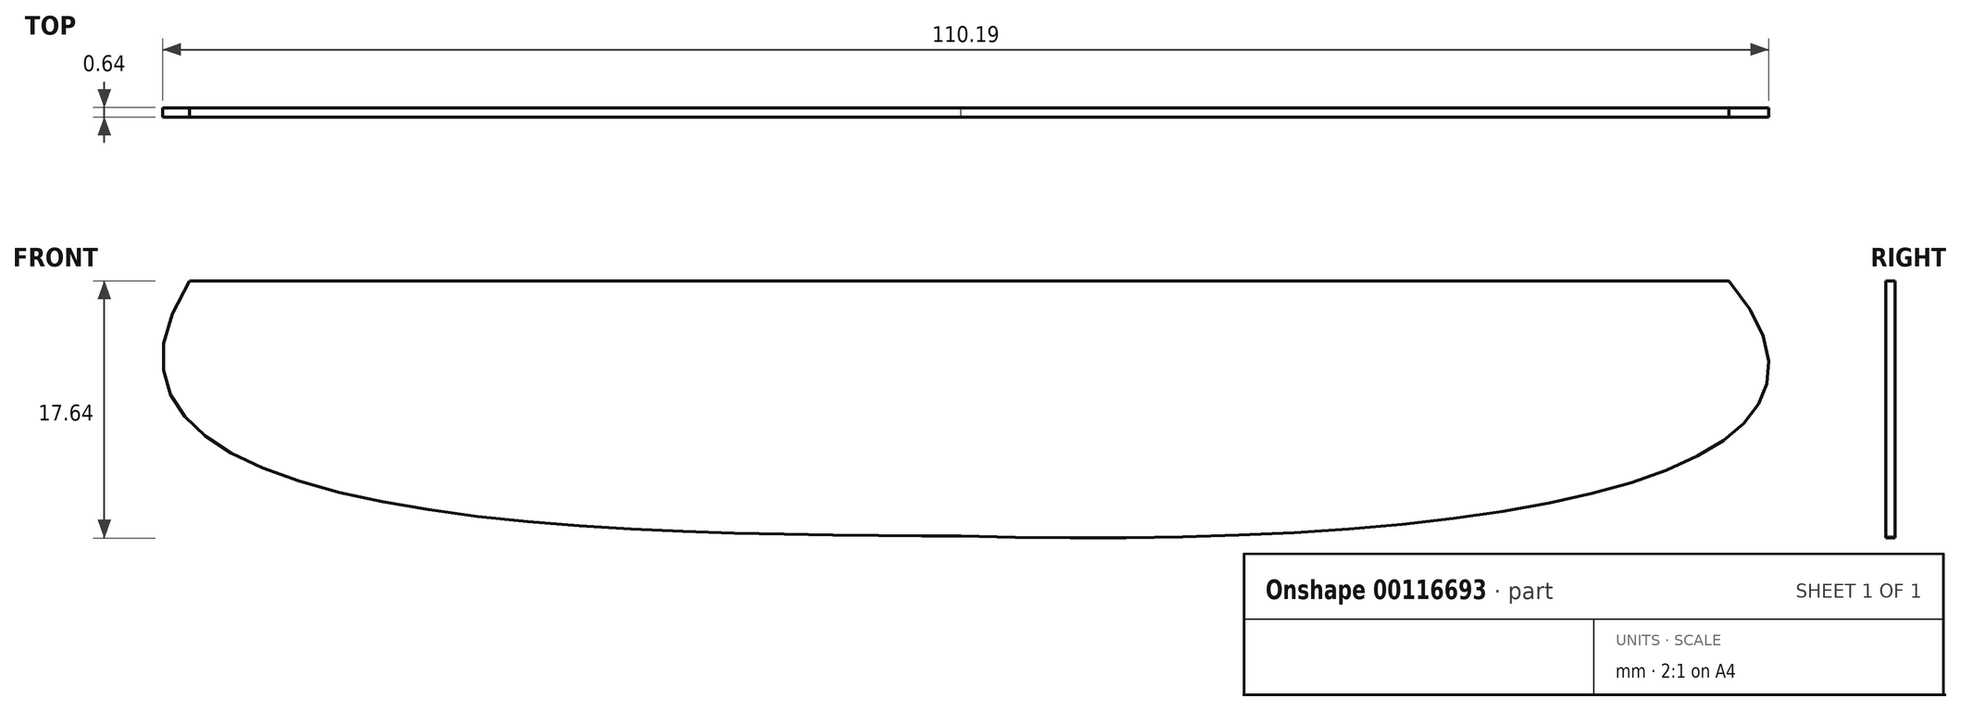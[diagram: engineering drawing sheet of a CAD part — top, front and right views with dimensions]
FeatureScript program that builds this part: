
annotation { "Feature Type Name" : "Feature", "Feature Type Description" : "" }
export const myFeature = defineFeature(function(context is Context, id is Id, definition is map)
    precondition{}
    {
        {
            var Q0;
            Q0=qCreatedBy(makeId("Front.planeOp"),FACE);
            var sketch = newSketch(context, id + "F0", { "sketchPlane" : qUnion([Q0])});
            skFitSpline(sketch, "E0", {"points": [v(52.68, 4.64) * mm, v(0, -12.87) * mm], "startDerivative": vector(39.8, -46.97) * mm, "endDerivative": vector(-84, 2.39) * mm});
            skLineSegment(sketch, "E1", {"start": v(-52.94, 4.64) * mm, "end": v(52.68, 4.64) * mm});
            skFitSpline(sketch, "E2", {"points": [v(0, -12.87) * mm, v(-52.94, 4.64) * mm], "startDerivative": vector(-59.13, 0.65) * mm, "endDerivative": vector(34.23, 54.14) * mm});
            skSolve(sketch);
        }
        {
            var Q0;
            Q0=makeQuery(id+"F0.imprint","IMPRINT",FACE,{"disambiguationData":[TD([[makeQuery(id+"F0.imprint","IMPRINT",EDGE,{"derivedFrom":sQuery(id+"F0.wireOp",EDGE,"E0")}),-1.0]])]});
            extrude(context, id + "F1", {"entities" : qUnion([Q0]), "endBound" : BoundingType.SYMMETRIC, "depth" : 0.64 * mm});
        }
    });
